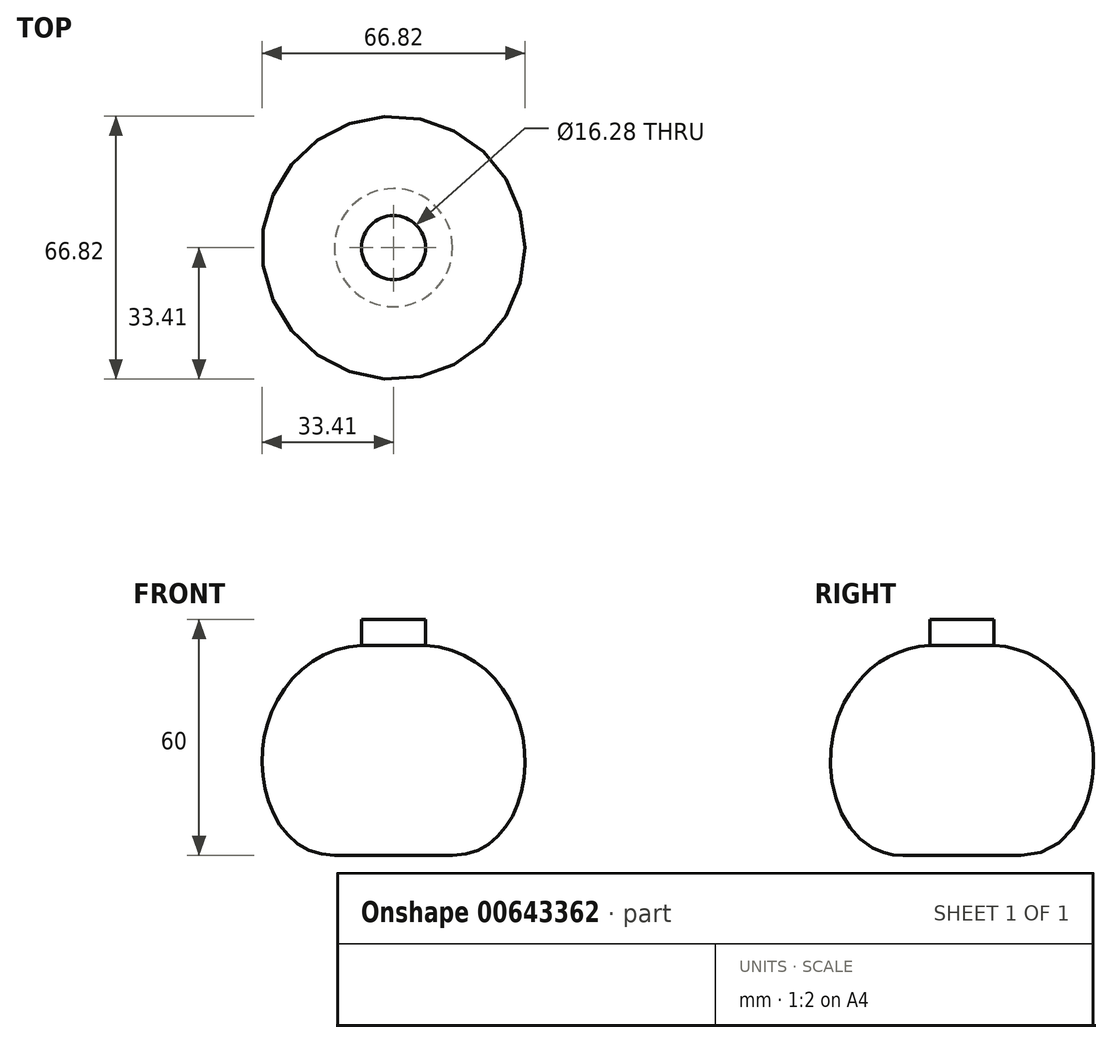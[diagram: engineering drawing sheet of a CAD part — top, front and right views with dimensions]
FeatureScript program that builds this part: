
annotation { "Feature Type Name" : "Feature", "Feature Type Description" : "" }
export const myFeature = defineFeature(function(context is Context, id is Id, definition is map)
    precondition{}
    {
        {
            var Q0;
            Q0=qCreatedBy(makeId("Front.planeOp"),FACE);
            var sketch = newSketch(context, id + "F0", { "sketchPlane" : qUnion([Q0])});
            skLineSegment(sketch, "E0", {"start": v(0, 0) * mm, "end": v(0, 60) * mm});
            skLineSegment(sketch, "E1", {"start": v(0, 0) * mm, "end": v(15, 0) * mm});
            skFitSpline(sketch, "E2", {"points": [v(15, 0) * mm, v(33.24, 27.4) * mm, v(8.14, 53.36) * mm], "startDerivative": vector(81.3, 0) * mm, "endDerivative": vector(-81.53, 4.1) * mm});
            skLineSegment(sketch, "E3", {"start": v(8.14, 53.36) * mm, "end": v(8.14, 60) * mm});
            skLineSegment(sketch, "E4", {"start": v(8.14, 60) * mm, "end": v(0, 60) * mm});
            skSolve(sketch);
        }
        {
            var Q0;
            Q0=sQuery(id+"F0.wireOp",EDGE,"E3");
            var Q1;
            Q1=sQuery(id+"F0.wireOp",EDGE,"E2");
            var Q2;
            Q2=sQuery(id+"F0.wireOp",EDGE,"E0");
            revolve(context, id + "F1", {"bodyType" : ToolBodyType.SURFACE, "surfaceEntities" : qUnion([Q0, Q1]), "axis" : qUnion([Q2]), "revolveType" : RevolveType.FULL});
        }
    });
